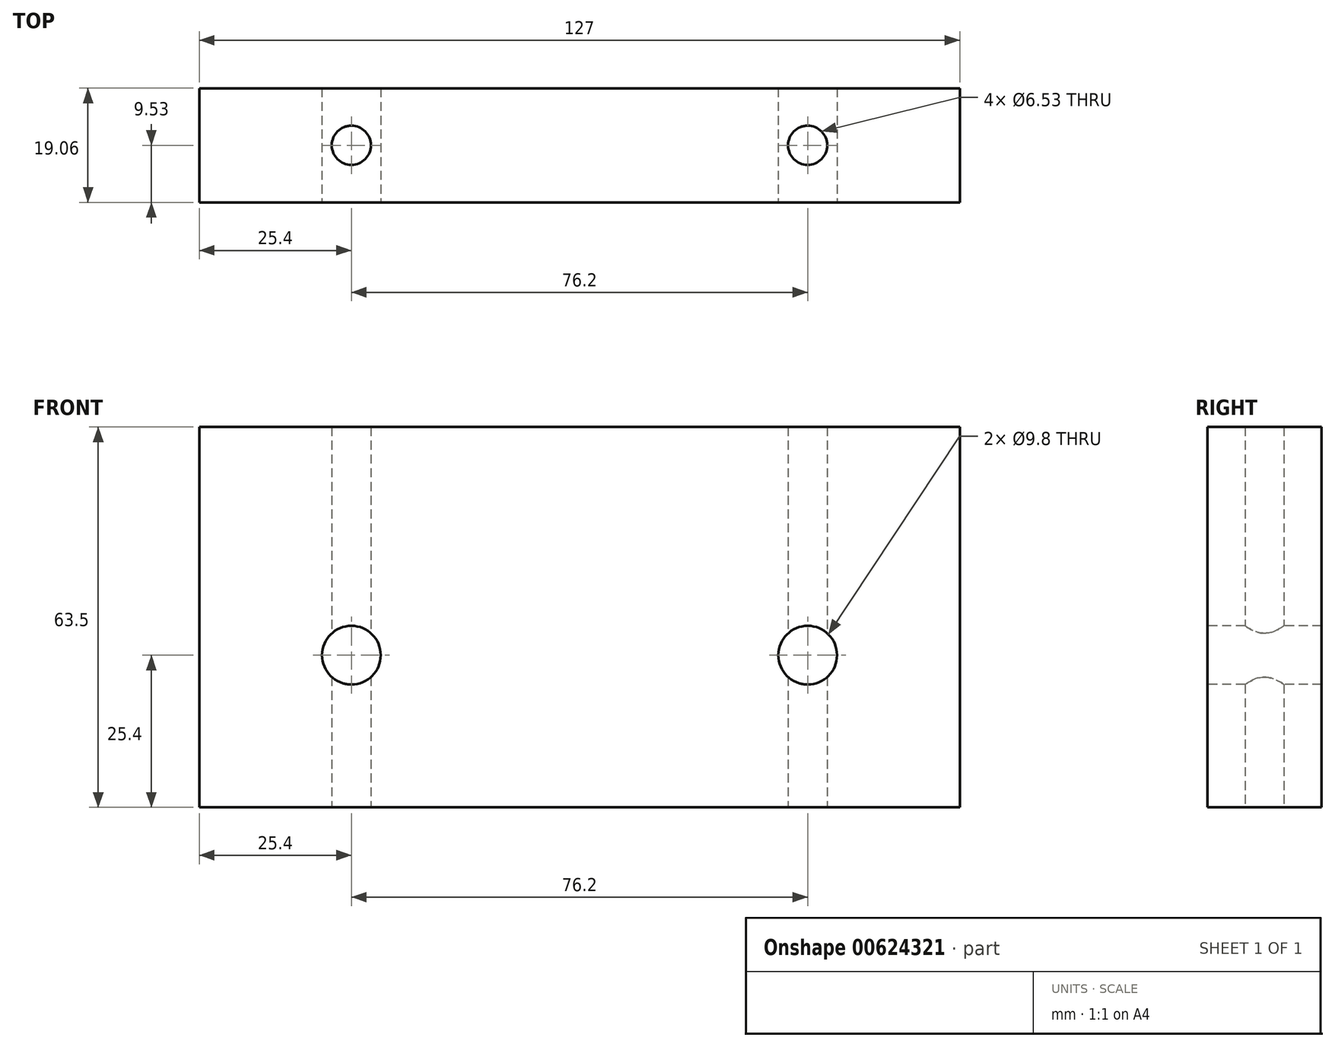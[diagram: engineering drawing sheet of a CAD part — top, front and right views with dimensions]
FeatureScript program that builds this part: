
annotation { "Feature Type Name" : "Feature", "Feature Type Description" : "" }
export const myFeature = defineFeature(function(context is Context, id is Id, definition is map)
    precondition{}
    {
        {
            var Q0;
            Q0=qCreatedBy(makeId("Front.planeOp"),FACE);
            var sketch = newSketch(context, id + "F0", { "sketchPlane" : qUnion([Q0])});
            skLineSegment(sketch, "E0.bottom", {"start": v(-63.5, 31.75) * mm, "end": v(63.5, 31.75) * mm});
            skLineSegment(sketch, "E0.top", {"start": v(-63.5, -31.75) * mm, "end": v(63.5, -31.75) * mm});
            skLineSegment(sketch, "E0.left", {"start": v(-63.5, 31.75) * mm, "end": v(-63.5, -31.75) * mm});
            skLineSegment(sketch, "E0.right", {"start": v(63.5, 31.75) * mm, "end": v(63.5, -31.75) * mm});
            skLineSegment(sketch, "E1", {"start": v(-63.5, 0) * mm, "end": v(63.5, 0) * mm, "construction": true});
            skLineSegment(sketch, "E2", {"start": v(0, 31.75) * mm, "end": v(0, -31.75) * mm, "construction": true});
            skSolve(sketch);
        }
        {
            var Q0;
            Q0=makeQuery(id+"F0.imprint","IMPRINT",FACE,{"disambiguationData":[TD([[makeQuery(id+"F0.imprint","IMPRINT",EDGE,{"derivedFrom":sQuery(id+"F0.wireOp",EDGE,"E0.bottom")}),-1.0]])]});
            extrude(context, id + "F1", {"entities" : qUnion([Q0]), "endBound" : BoundingType.SYMMETRIC, "depth" : 19.05 * mm, "offsetDistance" : 25.4 * mm});
        }
        {
            var Q0;
            Q0=makeQuery(id+"F1.opExtrude","CAP_FACE",FACE,{"disambiguationData":[OSD([sQuery(id+"F0.wireOp",EDGE,"E0.bottom"),sQuery(id+"F0.wireOp",EDGE,"E0.top"),sQuery(id+"F0.wireOp",EDGE,"E0.left"),sQuery(id+"F0.wireOp",EDGE,"E0.right")])],"isStart":false});
            var sketch = newSketch(context, id + "F2", { "sketchPlane" : qUnion([Q0])});
            skPoint(sketch, "E3", {"position": v(-38.1, -6.35) * mm});
            skPoint(sketch, "E4", {"position": v(38.1, -6.35) * mm});
            skSolve(sketch);
        }
        {
            var Q0;
            Q0=sQuery(id+"F2.wireOp",VERTEX,"E3");
            var Q1;
            Q1=sQuery(id+"F2.wireOp",VERTEX,"E4");
            var Q2;
            Q2=makeQuery(id+"F1.opExtrude","SWEPT_BODY",BODY,{"disambiguationData":[OSD([sQuery(id+"F0.wireOp",EDGE,"E0.bottom"),sQuery(id+"F0.wireOp",EDGE,"E0.top"),sQuery(id+"F0.wireOp",EDGE,"E0.left"),sQuery(id+"F0.wireOp",EDGE,"E0.right")])]});
            hole(context, id + "F3", {"style" : HoleStyle.SIMPLE, "endStyle" : HoleEndStyle.THROUGH, "standardTappedOrClearance" : lookupTablePath({ "standard" : "ANSI", "fit" : "Close", "size" : "3/8", "type" : "Clearance" }), "standardBlindInLast" : lookupTablePath({ "fit" : "Close", "standard" : "ANSI", "size" : "3/8", "type" : "Clearance" }), "holeDiameter" : 9.8 * mm, "majorDiameter" : 6.35 * mm, "isTappedThrough" : true, "tappedDepth" : 12.7 * mm, "tapClearance" : 3, "startFromSketch" : true, "locations" : qUnion([Q0, Q1]), "scope" : qUnion([Q2])});
        }
        {
            var Q0;
            Q0=makeQuery(id+"F1.opExtrude","SWEPT_FACE",FACE,{"disambiguationData":[OSD([sQuery(id+"F0.wireOp",EDGE,"E0.top")])]});
            var sketch = newSketch(context, id + "F4", { "sketchPlane" : qUnion([Q0])});
            skPoint(sketch, "E5", {"position": v(-38.1, 0) * mm});
            skPoint(sketch, "E6", {"position": v(38.1, 0) * mm});
            skSolve(sketch);
        }
        {
            var Q0;
            Q0=sQuery(id+"F4.wireOp",VERTEX,"E5");
            var Q1;
            Q1=sQuery(id+"F4.wireOp",VERTEX,"E6");
            var Q2;
            Q2=makeQuery(id+"F1.opExtrude","SWEPT_BODY",BODY,{"disambiguationData":[OSD([sQuery(id+"F0.wireOp",EDGE,"E0.bottom"),sQuery(id+"F0.wireOp",EDGE,"E0.top"),sQuery(id+"F0.wireOp",EDGE,"E0.left"),sQuery(id+"F0.wireOp",EDGE,"E0.right")])]});
            hole(context, id + "F5", {"style" : HoleStyle.SIMPLE, "endStyle" : HoleEndStyle.THROUGH, "standardTappedOrClearance" : lookupTablePath({ "standard" : "ANSI", "fit" : "Close", "size" : "1/4", "type" : "Clearance" }), "standardBlindInLast" : lookupTablePath({ "fit" : "Close", "standard" : "ANSI", "size" : "1/4", "type" : "Clearance" }), "holeDiameter" : 6.53 * mm, "majorDiameter" : 6.35 * mm, "isTappedThrough" : true, "tappedDepth" : 12.7 * mm, "tapClearance" : 3, "startFromSketch" : true, "locations" : qUnion([Q0, Q1]), "scope" : qUnion([Q2])});
        }
    });
